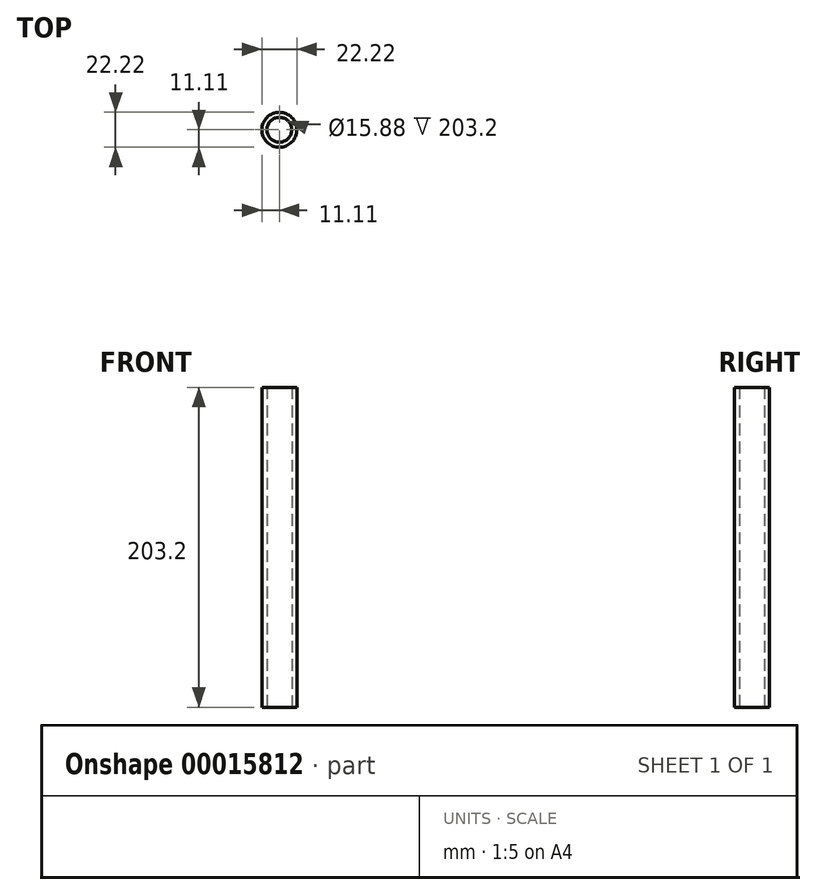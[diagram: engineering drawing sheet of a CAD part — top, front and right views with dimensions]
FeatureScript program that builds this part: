
annotation { "Feature Type Name" : "Feature", "Feature Type Description" : "" }
export const myFeature = defineFeature(function(context is Context, id is Id, definition is map)
    precondition{}
    {
        {
            var Q0;
            Q0=qCreatedBy(makeId("Top.planeOp"),FACE);
            var sketch = newSketch(context, id + "F0", { "sketchPlane" : qUnion([Q0])});
            skCircle(sketch, "E0", {"center": v(0, 0) * mm, "radius": 7.94 * mm});
            skCircle(sketch, "E1", {"center": v(0, 0) * mm, "radius": 11.11 * mm});
            skSolve(sketch);
        }
        {
            var Q0;
            Q0 = qSketchRegion(id + "F0", true);
            extrude(context, id + "F1", {"entities" : qUnion([Q0]), "depth" : 203.2 * mm});
        }
    });
